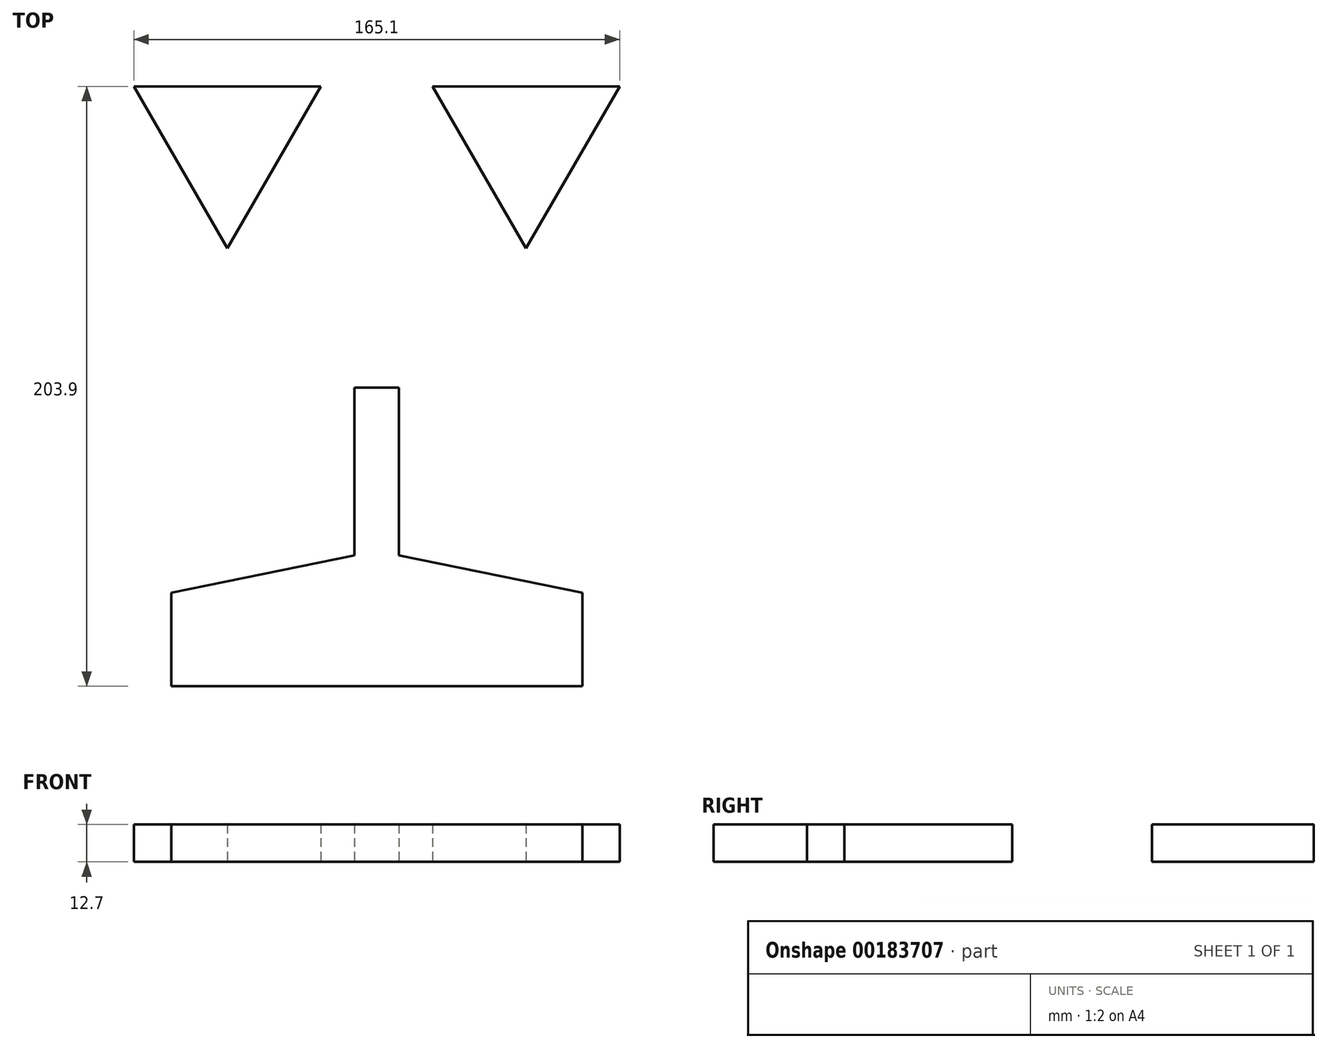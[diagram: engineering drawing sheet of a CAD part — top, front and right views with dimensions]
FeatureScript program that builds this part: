
annotation { "Feature Type Name" : "Feature", "Feature Type Description" : "" }
export const myFeature = defineFeature(function(context is Context, id is Id, definition is map)
    precondition{}
    {
        {
            var Q0;
            Q0=qCreatedBy(makeId("Top.planeOp"),FACE);
            var sketch = newSketch(context, id + "F0", { "sketchPlane" : qUnion([Q0])});
            skCircle(sketch, "E0.cCircle", {"center": v(-50.8, 50.8) * mm, "radius": 18.33 * mm, "construction": true});
            skLineSegment(sketch, "E0.0", {"start": v(-82.55, 69.13) * mm, "end": v(-19.05, 69.13) * mm});
            skLineSegment(sketch, "E0.1", {"start": v(-19.05, 69.13) * mm, "end": v(-50.8, 14.14) * mm});
            skLineSegment(sketch, "E0.2", {"start": v(-50.8, 14.14) * mm, "end": v(-82.55, 69.13) * mm});
            skPoint(sketch, "E0.0.midPoint", {"position": v(-50.8, 69.13) * mm});
            skLineSegment(sketch, "E1", {"start": v(0, 0) * mm, "end": v(0, 50.8) * mm, "construction": true});
            skLineSegment(sketch, "E2.MirrorCS", {"start": v(82.55, 69.13) * mm, "end": v(19.05, 69.13) * mm});
            skLineSegment(sketch, "E3.MirrorCS", {"start": v(50.8, 14.14) * mm, "end": v(82.55, 69.13) * mm});
            skLineSegment(sketch, "E4.MirrorCS", {"start": v(19.05, 69.13) * mm, "end": v(50.8, 14.14) * mm});
            skLineSegment(sketch, "E5.bottom", {"start": v(7.5, -33.3) * mm, "end": v(-7.5, -33.3) * mm});
            skLineSegment(sketch, "E5.top", {"start": v(7.5, -118.9) * mm, "end": v(-7.5, -118.9) * mm});
            skLineSegment(sketch, "E5.left", {"start": v(7.5, -33.3) * mm, "end": v(7.5, -118.9) * mm});
            skLineSegment(sketch, "E5.right", {"start": v(-7.5, -33.3) * mm, "end": v(-7.5, -118.9) * mm});
            skPoint(sketch, "E5.middle", {"position": v(0, -76.1) * mm});
            skLineSegment(sketch, "E6.bottom", {"start": v(-69.85, -103.02) * mm, "end": v(69.85, -103.02) * mm});
            skLineSegment(sketch, "E6.top", {"start": v(-69.85, -134.77) * mm, "end": v(69.85, -134.77) * mm});
            skLineSegment(sketch, "E6.left", {"start": v(-69.85, -103.02) * mm, "end": v(-69.85, -134.77) * mm});
            skLineSegment(sketch, "E6.right", {"start": v(69.85, -103.02) * mm, "end": v(69.85, -134.77) * mm});
            skPoint(sketch, "E6.middle", {"position": v(0, -118.9) * mm});
            skLineSegment(sketch, "E7", {"start": v(-69.85, -103.02) * mm, "end": v(-7.5, -90.32) * mm});
            skLineSegment(sketch, "E8.MirrorCS", {"start": v(69.85, -103.02) * mm, "end": v(7.5, -90.32) * mm});
            skSolve(sketch);
        }
        {
            var Q0;
            Q0=makeQuery(id+"F0.imprint","IMPRINT",FACE,{"disambiguationData":[TD([[makeQuery(id+"F0.imprint","IMPRINT",EDGE,{"derivedFrom":sQuery(id+"F0.wireOp",EDGE,"E0.0")}),-1.0]])]});
            var Q1;
            Q1=makeQuery(id+"F0.imprint","IMPRINT",FACE,{"disambiguationData":[TD([[makeQuery(id+"F0.imprint","IMPRINT",EDGE,{"derivedFrom":sQuery(id+"F0.wireOp",EDGE,"E2.MirrorCS")}),1.0]])]});
            var Q2;
            {var subQ1=sQuery(id+"F0.wireOp",EDGE,"E5.bottom");Q2=makeQuery(id+"F0.imprint","IMPRINT",FACE,{"disambiguationData":[TD([[makeQuery(id+"F0.imprint","IMPRINT",EDGE,{"derivedFrom":subQ1}),1.0]])]});}
            var Q3;
            {var subQ0=sQuery(id+"F0.wireOp",EDGE,"E7");Q3=makeQuery(id+"F0.imprint","IMPRINT",FACE,{"disambiguationData":[TD([[makeQuery(id+"F0.imprint","IMPRINT",EDGE,{"derivedFrom":subQ0}),-1.0]])]});}
            var Q4;
            {var subQ4=sQuery(id+"F0.wireOp",EDGE,"E5.top");Q4=makeQuery(id+"F0.imprint","IMPRINT",FACE,{"disambiguationData":[TD([[makeQuery(id+"F0.imprint","IMPRINT",EDGE,{"derivedFrom":subQ4}),1.0]])]});}
            var Q5;
            {var subQ0=sQuery(id+"F0.wireOp",EDGE,"E8.MirrorCS");Q5=makeQuery(id+"F0.imprint","IMPRINT",FACE,{"disambiguationData":[TD([[makeQuery(id+"F0.imprint","IMPRINT",EDGE,{"derivedFrom":subQ0}),1.0]])]});}
            var Q6;
            {var subQ0=sQuery(id+"F0.wireOp",EDGE,"E5.top");Q6=makeQuery(id+"F0.imprint","IMPRINT",FACE,{"disambiguationData":[TD([[makeQuery(id+"F0.imprint","IMPRINT",EDGE,{"derivedFrom":subQ0}),-1.0]])]});}
            extrude(context, id + "F1", {"entities" : qUnion([Q0, Q1, Q2, Q3, Q4, Q5, Q6]), "depth" : 12.7 * mm});
        }
    });
